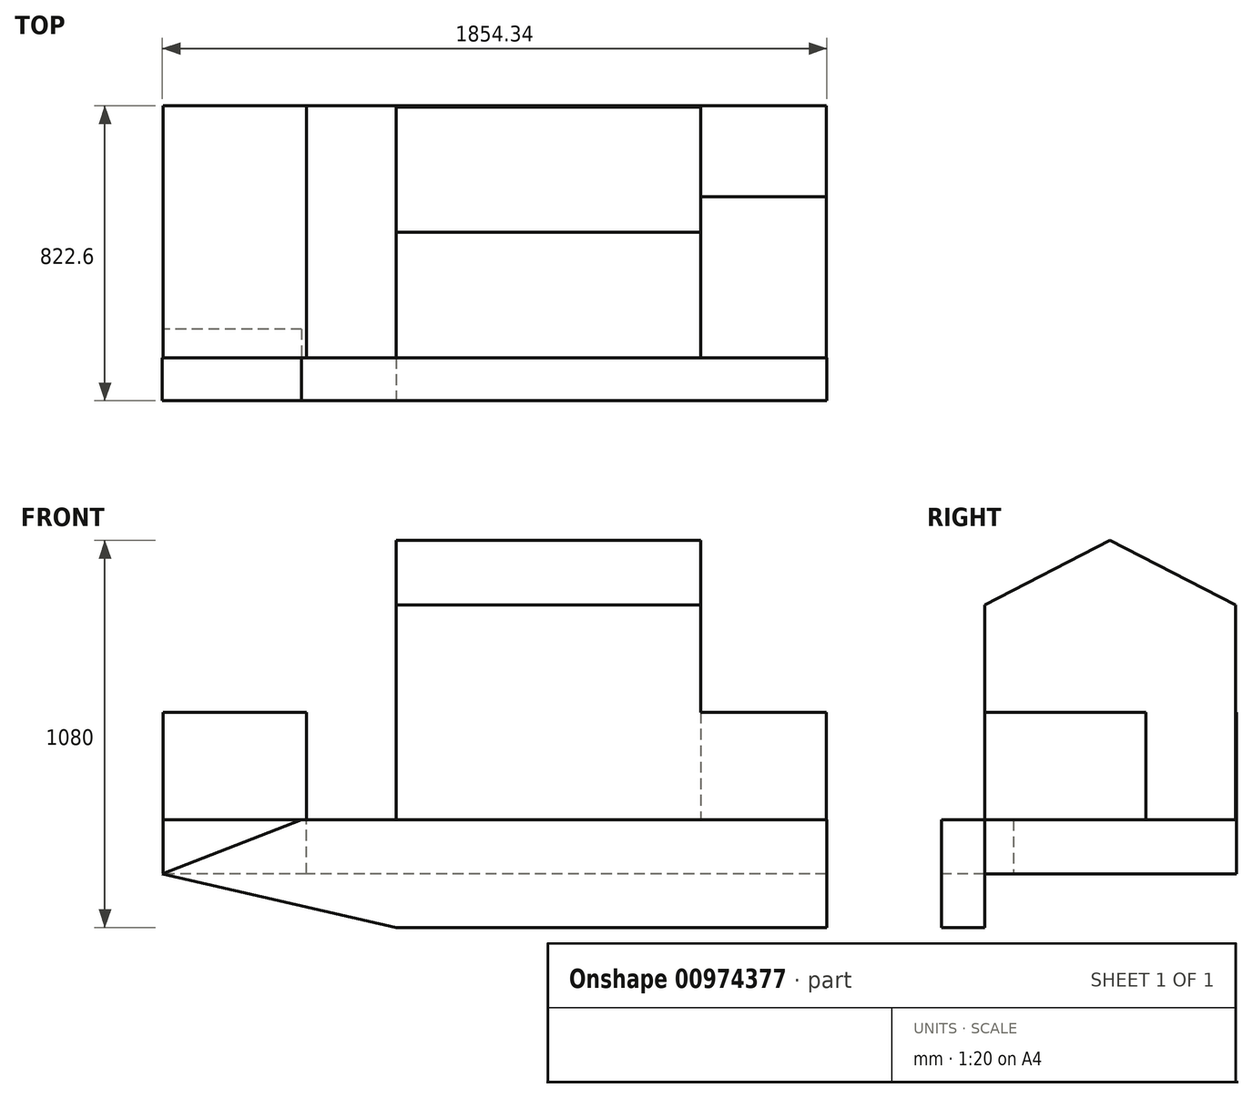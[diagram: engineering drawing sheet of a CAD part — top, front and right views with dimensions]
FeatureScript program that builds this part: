
annotation { "Feature Type Name" : "Feature", "Feature Type Description" : "" }
export const myFeature = defineFeature(function(context is Context, id is Id, definition is map)
    precondition{}
    {
        {
            var Q0;
            Q0=qCreatedBy(makeId("Top.planeOp"),FACE);
            var sketch = newSketch(context, id + "F0", { "sketchPlane" : qUnion([Q0])});
            skLineSegment(sketch, "E0.bottom", {"start": v(0, 0) * mm, "end": v(1200, 0) * mm});
            skLineSegment(sketch, "E0.top", {"start": v(0, 700) * mm, "end": v(850, 700) * mm});
            skLineSegment(sketch, "E0.left", {"start": v(0, 0) * mm, "end": v(0, 700) * mm});
            skLineSegment(sketch, "E0.right", {"start": v(1200, 0) * mm, "end": v(1200, 450) * mm});
            skLineSegment(sketch, "E1.left", {"start": v(1200, 0) * mm, "end": v(1200, 150.84) * mm});
            skLineSegment(sketch, "E2.top", {"start": v(1200, 450) * mm, "end": v(850, 450) * mm});
            skLineSegment(sketch, "E2.right", {"start": v(850, 700) * mm, "end": v(850, 450) * mm});
            skLineSegment(sketch, "E3.bottom", {"start": v(-250, 0) * mm, "end": v(-650, 0) * mm});
            skLineSegment(sketch, "E3.top", {"start": v(-250, 702.98) * mm, "end": v(-650, 702.98) * mm});
            skLineSegment(sketch, "E3.left", {"start": v(-250, 0) * mm, "end": v(-250, 702.98) * mm});
            skLineSegment(sketch, "E3.right", {"start": v(-650, 0) * mm, "end": v(-650, 702.98) * mm});
            skSolve(sketch);
        }
        {
            var Q0;
            Q0=makeQuery(id+"F0.imprint","IMPRINT",FACE,{"disambiguationData":[TD([[makeQuery(id+"F0.imprint","IMPRINT",EDGE,{"derivedFrom":sQuery(id+"F0.wireOp",EDGE,"E3.bottom")}),-1.0]])]});
            extrude(context, id + "F1", {"entities" : qUnion([Q0]), "depth" : 300 * mm, "offsetDistance" : 25 * mm});
        }
        {
            var Q0;
            Q0=makeQuery(id+"F0.imprint","IMPRINT",FACE,{"disambiguationData":[TD([[makeQuery(id+"F0.imprint","IMPRINT",EDGE,{"derivedFrom":sQuery(id+"F0.wireOp",EDGE,"E0.bottom")}),1.0]])]});
            extrude(context, id + "F2", {"entities" : qUnion([Q0]), "depth" : 300 * mm, "offsetDistance" : 25 * mm});
        }
        {
            var Q0;
            Q0=makeQuery(id+"F2.opExtrude","CAP_FACE",FACE,{"disambiguationData":[OSD([sQuery(id+"F0.wireOp",EDGE,"E0.bottom"),sQuery(id+"F0.wireOp",EDGE,"E0.top"),sQuery(id+"F0.wireOp",EDGE,"E0.left"),sQuery(id+"F0.wireOp",EDGE,"E0.right"),sQuery(id+"F0.wireOp",EDGE,"E1.left"),sQuery(id+"F0.wireOp",EDGE,"E2.top"),sQuery(id+"F0.wireOp",EDGE,"E2.right")])],"isStart":false});
            var sketch = newSketch(context, id + "F3", { "sketchPlane" : qUnion([Q0])});
            skLineSegment(sketch, "E4.bottom", {"start": v(0, 0) * mm, "end": v(850, 0) * mm});
            skLineSegment(sketch, "E4.top", {"start": v(0, 700) * mm, "end": v(850, 700) * mm});
            skLineSegment(sketch, "E4.left", {"start": v(0, 0) * mm, "end": v(0, 700) * mm});
            skLineSegment(sketch, "E4.right", {"start": v(850, 0) * mm, "end": v(850, 700) * mm});
            skSolve(sketch);
        }
        {
            var Q0;
            {var subQ2=sQuery(id+"F3.wireOp",EDGE,"E4.bottom");Q0=makeQuery(id+"F3.imprint","IMPRINT",FACE,{"disambiguationData":[TD([[makeQuery(id+"F3.imprint","IMPRINT",EDGE,{"derivedFrom":subQ2}),1.0]])]});}
            extrude(context, id + "F4", {"entities" : qUnion([Q0]), "operationType" : NewBodyOperationType.ADD, "depth" : 300 * mm, "offsetDistance" : 25 * mm});
        }
        {
            var Q0;
            Q0=makeQuery(id+"F4.opExtrude","CAP_FACE",FACE,{"disambiguationData":[OSD([sQuery(id+"F3.wireOp",EDGE,"E4.bottom"),sQuery(id+"F3.wireOp",EDGE,"E4.top"),sQuery(id+"F3.wireOp",EDGE,"E4.left"),sQuery(id+"F3.wireOp",EDGE,"E4.right")])],"isStart":false});
            var sketch = newSketch(context, id + "F5", { "sketchPlane" : qUnion([Q0])});
            skLineSegment(sketch, "E5.bottom", {"start": v(0, 350) * mm, "end": v(850, 350) * mm});
            skLineSegment(sketch, "E5.top", {"start": v(0, 0) * mm, "end": v(850, 0) * mm});
            skLineSegment(sketch, "E5.left", {"start": v(0, 350) * mm, "end": v(0, 0) * mm});
            skLineSegment(sketch, "E5.right", {"start": v(850, 350) * mm, "end": v(850, 0) * mm});
            skLineSegment(sketch, "E6.bottom", {"start": v(0, 700) * mm, "end": v(850, 700) * mm});
            skLineSegment(sketch, "E6.left", {"start": v(0, 700) * mm, "end": v(0, 350) * mm});
            skLineSegment(sketch, "E6.right", {"start": v(850, 700) * mm, "end": v(850, 350) * mm});
            skSolve(sketch);
        }
        {
            var Q0;
            Q0=makeQuery(id+"F5.imprint","IMPRINT",FACE,{"disambiguationData":[TD([[makeQuery(id+"F5.imprint","IMPRINT",EDGE,{"derivedFrom":sQuery(id+"F5.wireOp",EDGE,"E5.bottom")}),-1.0]])]});
            var Q1;
            Q1 = qSketchRegion(id + "F7", true);
            extrude(context, id + "F6", {"entities" : qUnion([Q0, Q1]), "operationType" : NewBodyOperationType.ADD, "depth" : 180 * mm, "offsetDistance" : 25 * mm});
        }
        {
            var Q0;
            Q0=makeQuery(id+"F6.boolean.opBoolean","MERGE",FACE,{"derivedFrom":[makeQuery(id+"F4.boolean.opBoolean","MERGE",FACE,{"derivedFrom":[makeQuery(id+"F2.opExtrude","SWEPT_FACE",FACE,{"disambiguationData":[OSD([sQuery(id+"F0.wireOp",EDGE,"E0.left")])]}),makeQuery(id+"F4.opExtrude","SWEPT_FACE",FACE,{"disambiguationData":[OSD([sQuery(id+"F3.wireOp",EDGE,"E4.left")])]})]}),makeQuery(id+"F6.opExtrude","SWEPT_FACE",FACE,{"disambiguationData":[OSD([sQuery(id+"F5.wireOp",EDGE,"E5.left")])]})]});
            var sketch = newSketch(context, id + "F7", { "sketchPlane" : qUnion([Q0])});
            skLineSegment(sketch, "E7", {"start": v(-350, 780) * mm, "end": v(0, 600) * mm});
            skPoint(sketch, "E7.endSnap0", {"position": v(-350, 600) * mm});
            skLineSegment(sketch, "E8", {"start": v(0, 600) * mm, "end": v(0, 780) * mm});
            skLineSegment(sketch, "E9", {"start": v(0, 780) * mm, "end": v(-350, 780) * mm});
            skSolve(sketch);
        }
        {
            var Q0;
            Q0=makeQuery(id+"F7.imprint","IMPRINT",FACE,{"disambiguationData":[TD([[makeQuery(id+"F7.imprint","IMPRINT",EDGE,{"derivedFrom":sQuery(id+"F7.wireOp",EDGE,"E7")}),1.0]])]});
            extrude(context, id + "F8", {"entities" : qUnion([Q0]), "operationType" : NewBodyOperationType.REMOVE, "oppositeDirection" : true, "depth" : 1000 * mm, "offsetDistance" : 25 * mm});
        }
        {
            var Q0;
            Q0=makeQuery(id+"F5.imprint","IMPRINT",FACE,{"disambiguationData":[TD([[makeQuery(id+"F5.imprint","IMPRINT",EDGE,{"derivedFrom":sQuery(id+"F5.wireOp",EDGE,"E6.bottom")}),-1.0]])]});
            extrude(context, id + "F9", {"entities" : qUnion([Q0]), "operationType" : NewBodyOperationType.ADD, "depth" : 180 * mm, "offsetDistance" : 25 * mm});
        }
        {
            var Q0;
            Q0 = qSketchRegion(id + "F5", true);
            var Q1;
            Q1=makeQuery(id+"F4.opExtrude","CAP_FACE",FACE,{"disambiguationData":[OSD([sQuery(id+"F3.wireOp",EDGE,"E4.bottom"),sQuery(id+"F3.wireOp",EDGE,"E4.top"),sQuery(id+"F3.wireOp",EDGE,"E4.left"),sQuery(id+"F3.wireOp",EDGE,"E4.right")])],"isStart":false});
            extrude(context, id + "F10", {"entities" : qUnion([Q0, Q1]), "operationType" : NewBodyOperationType.ADD, "depth" : 180 * mm, "offsetDistance" : 25 * mm});
        }
        {
            var Q0;
            Q0=makeQuery(id+"F7.imprint","IMPRINT",FACE,{"disambiguationData":[TD([[makeQuery(id+"F7.imprint","IMPRINT",EDGE,{"derivedFrom":sQuery(id+"F7.wireOp",EDGE,"E7")}),1.0]])]});
            extrude(context, id + "F11", {"entities" : qUnion([Q0]), "operationType" : NewBodyOperationType.REMOVE, "oppositeDirection" : true, "depth" : 1000 * mm, "offsetDistance" : 25 * mm});
        }
        {
            var Q0;
            {var subQ0=sQuery(id+"F5.wireOp",EDGE,"E6.left");Q0=makeQuery(id+"F10.boolean.opBoolean","MERGE",FACE,{"derivedFrom":[makeQuery(id+"F9.boolean.opBoolean","MERGE",FACE,{"derivedFrom":[makeQuery(id+"F4.boolean.opBoolean","MERGE",FACE,{"derivedFrom":[makeQuery(id+"F2.opExtrude","SWEPT_FACE",FACE,{"disambiguationData":[OSD([sQuery(id+"F0.wireOp",EDGE,"E0.left")])]}),makeQuery(id+"F4.opExtrude","SWEPT_FACE",FACE,{"disambiguationData":[OSD([sQuery(id+"F3.wireOp",EDGE,"E4.left")])]})]}),makeQuery(id+"F9.opExtrude","SWEPT_FACE",FACE,{"disambiguationData":[OSD([subQ0])]})]}),makeQuery(id+"F10.opExtrude","SWEPT_FACE",FACE,{"disambiguationData":[OSD([sQuery(id+"F5.wireOp",EDGE,"E5.left"),subQ0])]})]});}
            var sketch = newSketch(context, id + "F12", { "sketchPlane" : qUnion([Q0])});
            skLineSegment(sketch, "E10", {"start": v(-350, 780) * mm, "end": v(-700, 600) * mm});
            skLineSegment(sketch, "E11", {"start": v(-700, 600) * mm, "end": v(-700, 780) * mm});
            skLineSegment(sketch, "E12", {"start": v(-700, 780) * mm, "end": v(-350, 780) * mm});
            skSolve(sketch);
        }
        {
            var Q0;
            Q0 = qSketchRegion(id + "F12", true);
            extrude(context, id + "F13", {"entities" : qUnion([Q0]), "operationType" : NewBodyOperationType.REMOVE, "oppositeDirection" : true, "depth" : 10000 * mm, "offsetDistance" : 25 * mm});
        }
        {
            var Q0;
            Q0=qCreatedBy(makeId("Top.planeOp"),FACE);
            var sketch = newSketch(context, id + "F14", { "sketchPlane" : qUnion([Q0])});
            skLineSegment(sketch, "E13.bottom", {"start": v(1202.22, 0) * mm, "end": v(-652.12, 0) * mm});
            skLineSegment(sketch, "E13.top", {"start": v(1202.22, -119.62) * mm, "end": v(-652.12, -119.62) * mm});
            skLineSegment(sketch, "E13.left", {"start": v(1202.22, 0) * mm, "end": v(1202.22, -119.62) * mm});
            skLineSegment(sketch, "E13.right", {"start": v(-652.12, 0) * mm, "end": v(-652.12, -119.62) * mm});
            skSolve(sketch);
        }
        {
            var Q0;
            Q0 = qSketchRegion(id + "F14", true);
            extrude(context, id + "F15", {"entities" : qUnion([Q0]), "oppositeDirection" : true, "depth" : 300 * mm, "offsetDistance" : 25 * mm});
        }
        {
            var Q0;
            Q0=makeQuery(id+"F15.opExtrude","SWEPT_FACE",FACE,{"disambiguationData":[OSD([sQuery(id+"F14.wireOp",EDGE,"E13.top")])]});
            var sketch = newSketch(context, id + "F16", { "sketchPlane" : qUnion([Q0])});
            skLineSegment(sketch, "E14", {"start": v(-652.12, -150) * mm, "end": v(0, -300) * mm});
            skLineSegment(sketch, "E15", {"start": v(0, -300) * mm, "end": v(-652.12, -300) * mm});
            skLineSegment(sketch, "E16", {"start": v(-652.12, -300) * mm, "end": v(-652.12, -150) * mm});
            skLineSegment(sketch, "E17", {"start": v(-652.12, -150) * mm, "end": v(-263.49, 0) * mm});
            skLineSegment(sketch, "E18", {"start": v(-263.49, 0) * mm, "end": v(-652.12, 0) * mm});
            skLineSegment(sketch, "E19", {"start": v(-652.12, 0) * mm, "end": v(-652.12, -150) * mm});
            skSolve(sketch);
        }
        {
            var Q0;
            Q0 = qSketchRegion(id + "F16", true);
            extrude(context, id + "F17", {"entities" : qUnion([Q0]), "operationType" : NewBodyOperationType.REMOVE, "oppositeDirection" : true, "depth" : 200 * mm, "offsetDistance" : 25 * mm});
        }
        {
            var Q0;
            Q0 = qSketchRegion(id + "F16", true);
            extrude(context, id + "F18", {"entities" : qUnion([Q0]), "operationType" : NewBodyOperationType.REMOVE, "oppositeDirection" : true, "depth" : 200 * mm, "offsetDistance" : 25 * mm});
        }
        {
            var Q0;
            Q0=makeQuery(id+"F1.opExtrude","CAP_FACE",FACE,{"disambiguationData":[OSD([sQuery(id+"F0.wireOp",EDGE,"E3.bottom"),sQuery(id+"F0.wireOp",EDGE,"E3.top"),sQuery(id+"F0.wireOp",EDGE,"E3.left"),sQuery(id+"F0.wireOp",EDGE,"E3.right")])],"isStart":true});
            var sketch = newSketch(context, id + "F19", { "sketchPlane" : qUnion([Q0])});
            skLineSegment(sketch, "E20.bottom", {"start": v(-650, 0) * mm, "end": v(-250, 0) * mm});
            skLineSegment(sketch, "E20.top", {"start": v(-650, -702.98) * mm, "end": v(-250, -702.98) * mm});
            skLineSegment(sketch, "E20.left", {"start": v(-650, 0) * mm, "end": v(-650, -702.98) * mm});
            skLineSegment(sketch, "E20.right", {"start": v(-250, 0) * mm, "end": v(-250, -702.98) * mm});
            skSolve(sketch);
        }
        {
            var Q0;
            Q0 = qSketchRegion(id + "F19", true);
            extrude(context, id + "F20", {"entities" : qUnion([Q0]), "depth" : 150 * mm, "offsetDistance" : 25 * mm});
        }
        {
            var Q0;
            Q0=makeQuery(id+"F20.opExtrude","SWEPT_FACE",FACE,{"disambiguationData":[OSD([sQuery(id+"F19.wireOp",EDGE,"E20.right")])]});
            var sketch = newSketch(context, id + "F21", { "sketchPlane" : qUnion([Q0])});
            skLineSegment(sketch, "E21.bottom", {"start": v(0, 0) * mm, "end": v(702.98, 0) * mm});
            skLineSegment(sketch, "E21.top", {"start": v(0, -150) * mm, "end": v(702.98, -150) * mm});
            skLineSegment(sketch, "E21.left", {"start": v(0, 0) * mm, "end": v(0, -150) * mm});
            skLineSegment(sketch, "E21.right", {"start": v(702.98, 0) * mm, "end": v(702.98, -150) * mm});
            skSolve(sketch);
        }
        {
            var Q0;
            Q0 = qSketchRegion(id + "F21", true);
            extrude(context, id + "F22", {"entities" : qUnion([Q0]), "depth" : 1450 * mm, "offsetDistance" : 25 * mm});
        }
        {
            var Q0;
            Q0 = qSketchRegion(id + "F16", true);
            extrude(context, id + "F23", {"entities" : qUnion([Q0]), "operationType" : NewBodyOperationType.REMOVE, "oppositeDirection" : true, "depth" : 200 * mm, "offsetDistance" : 25 * mm});
        }
    });
